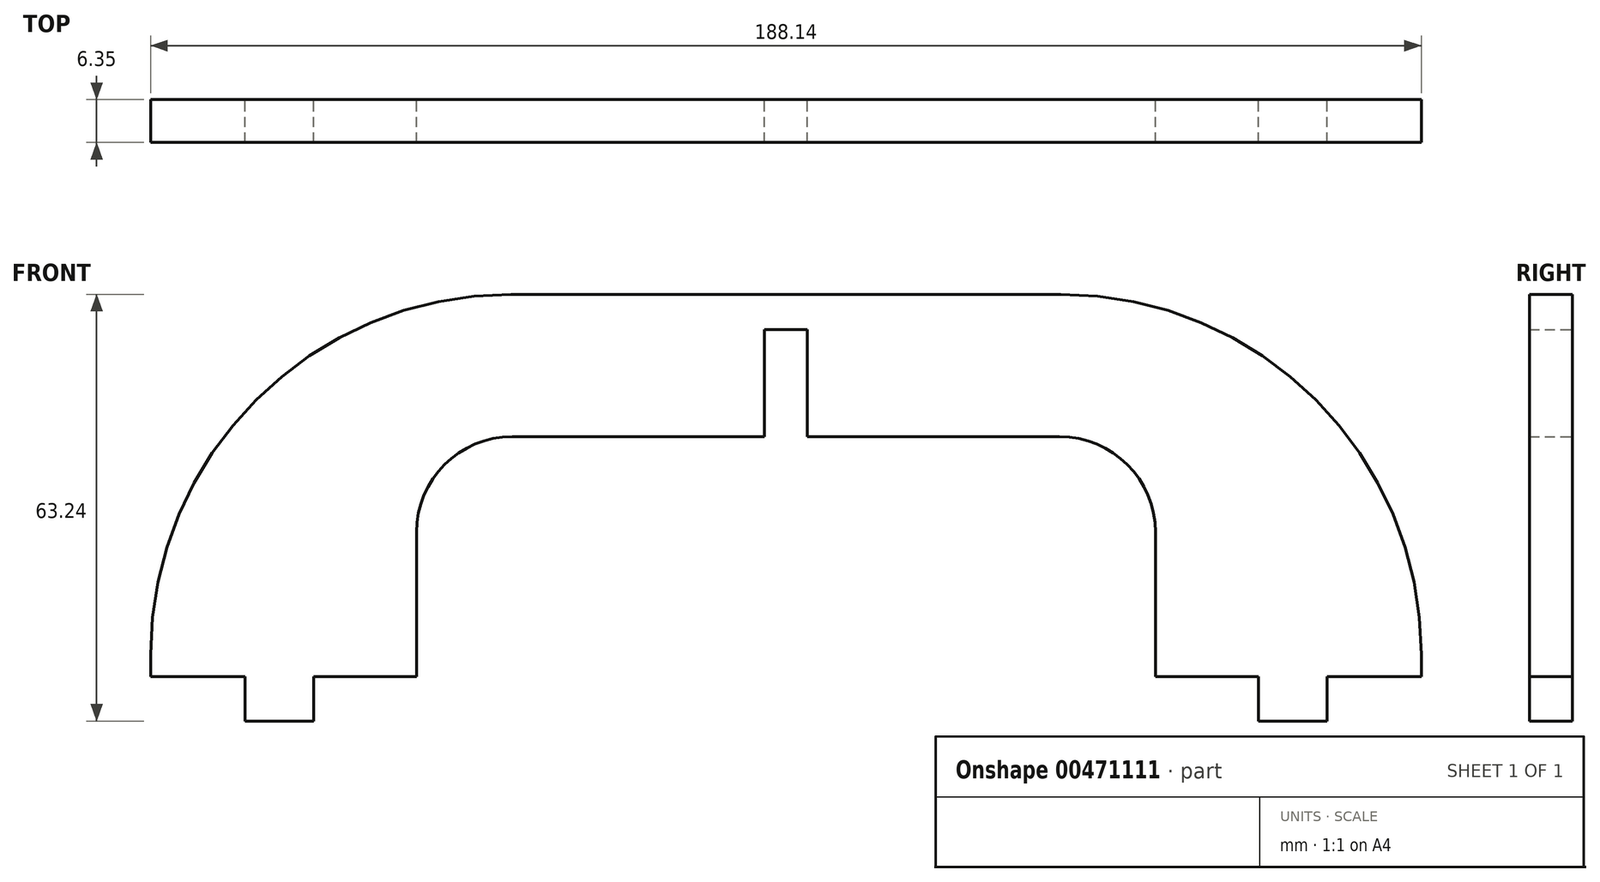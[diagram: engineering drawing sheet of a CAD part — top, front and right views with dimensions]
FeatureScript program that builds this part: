
annotation { "Feature Type Name" : "Feature", "Feature Type Description" : "" }
export const myFeature = defineFeature(function(context is Context, id is Id, definition is map)
    precondition{}
    {
        {
            var Q0;
            Q0=qCreatedBy(makeId("Front.planeOp"),FACE);
            var sketch = newSketch(context, id + "F0", { "sketchPlane" : qUnion([Q0])});
            skLineSegment(sketch, "E0", {"start": v(-69.94, 0) * mm, "end": v(-69.94, -6.6) * mm});
            skLineSegment(sketch, "E1", {"start": v(-69.94, -6.6) * mm, "end": v(-80.1, -6.6) * mm});
            skLineSegment(sketch, "E2", {"start": v(-80.1, -6.6) * mm, "end": v(-80.1, 0) * mm});
            skLineSegment(sketch, "E3", {"start": v(-80.1, 0) * mm, "end": v(-94.07, 0) * mm});
            skLineSegment(sketch, "E4", {"start": v(-69.94, 0) * mm, "end": v(-54.7, 0) * mm});
            skLineSegment(sketch, "E5", {"start": v(-54.7, 0) * mm, "end": v(-54.7, 21.37) * mm});
            skLineSegment(sketch, "E6", {"start": v(0, -3.84) * mm, "end": v(0, 119.5) * mm, "construction": true});
            skLineSegment(sketch, "E7", {"start": v(-40.51, 35.56) * mm, "end": v(-3.17, 35.56) * mm});
            skLineSegment(sketch, "E8", {"start": v(-94.07, 0) * mm, "end": v(-94.07, 3.27) * mm});
            skLineSegment(sketch, "E9", {"start": v(-3.17, 35.56) * mm, "end": v(-3.17, 51.4) * mm});
            skPoint(sketch, "E10.visualSharp", {"position": v(-94.07, 56.64) * mm});
            skArc(sketch, "E10.filletArc", {"start": v(-40.7, 56.64) * mm, "mid": v(-78.44, 41) * mm, "end": v(-94.07, 3.27) * mm});
            skPoint(sketch, "E11.visualSharp", {"position": v(-54.7, 35.56) * mm});
            skArc(sketch, "E11.filletArc", {"start": v(-40.51, 35.56) * mm, "mid": v(-50.55, 31.4) * mm, "end": v(-54.7, 21.37) * mm});
            skLineSegment(sketch, "E12.MirrorCS", {"start": v(94.07, 0) * mm, "end": v(94.07, 3.27) * mm});
            skLineSegment(sketch, "E13.MirrorCS", {"start": v(69.94, 0) * mm, "end": v(54.7, 0) * mm});
            skLineSegment(sketch, "E14.MirrorCS", {"start": v(69.94, -6.6) * mm, "end": v(80.1, -6.6) * mm});
            skLineSegment(sketch, "E15.MirrorCS", {"start": v(80.1, -6.6) * mm, "end": v(80.1, 0) * mm});
            skLineSegment(sketch, "E16.MirrorCS", {"start": v(54.7, 0) * mm, "end": v(54.7, 21.37) * mm});
            skLineSegment(sketch, "E17.MirrorCS", {"start": v(40.51, 35.56) * mm, "end": v(3.17, 35.56) * mm});
            skLineSegment(sketch, "E18.MirrorCS", {"start": v(3.17, 35.56) * mm, "end": v(3.17, 51.4) * mm});
            skArc(sketch, "E19.MirrorCS", {"start": v(40.7, 56.64) * mm, "mid": v(78.44, 41) * mm, "end": v(94.07, 3.27) * mm});
            skArc(sketch, "E20.MirrorCS", {"start": v(40.51, 35.56) * mm, "mid": v(50.55, 31.4) * mm, "end": v(54.7, 21.37) * mm});
            skLineSegment(sketch, "E21.MirrorCS", {"start": v(69.94, 0) * mm, "end": v(69.94, -6.6) * mm});
            skLineSegment(sketch, "E22.MirrorCS", {"start": v(80.1, 0) * mm, "end": v(94.07, 0) * mm});
            skLineSegment(sketch, "E23", {"start": v(-3.17, 51.4) * mm, "end": v(3.17, 51.4) * mm});
            skLineSegment(sketch, "E24", {"start": v(-40.7, 56.64) * mm, "end": v(40.7, 56.64) * mm});
            skSolve(sketch);
        }
        {
            var Q0;
            Q0=makeQuery(id+"F0.imprint","IMPRINT",FACE,{"disambiguationData":[TD([[makeQuery(id+"F0.imprint","IMPRINT",EDGE,{"derivedFrom":sQuery(id+"F0.wireOp",EDGE,"E0")}),-1.0]])]});
            extrude(context, id + "F1", {"entities" : qUnion([Q0]), "depth" : 6.35 * mm});
        }
    });
